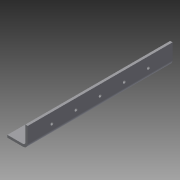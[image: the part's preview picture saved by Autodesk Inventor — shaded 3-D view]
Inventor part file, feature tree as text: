
AUTODESK INVENTOR PART (.ipt)
format: ipt  version: 2015 SP1 (Build 190203100, 203)  size: 133,632 bytes
history: native  units: in
note: dims shown in document units (in); Inventor stores cm internally (conversion verified against a paired STEP export)
features: sheet_metal_op x4, sketch x4, other x3, hole x2
ambient origin geometry x8: Origin, YZ Plane, XZ Plane, XY Plane, X Axis, Y Axis, Z Axis, Center Point
bodies: Solid1 (feature_tree)
feature tree (13):
  other  "<userpath>\Documents\2015 Offseason Chassis\West Coast Chassis Fall 2015\rivet(rv).xlsx"
  sheet_metal_op  "Face1"
  sheet_metal_op  "Flange1"
  hole  "Hole1"  [1 undecoded]
  hole  "Hole2"  [1 undecoded]
  sketch  "Sketch1"  dims[d0=1.0in d1=7.1in]
  other  "Plate1"
  sketch  "Sketch2"  dims[d2=0.12in d3=0.12in]
  other  "Plate2"
  sheet_metal_op  "Bend1"
  sheet_metal_op  "Corner1"
  sketch  "Sketch3"  dims[d4=0.06in]
  sketch  "Sketch4"  dims[d5=0.24in d6=0.12in d7=1.0in d8=90.0deg d9=0.12in d10=0.48in d11=0.12in d12=0.12in d13=0.5in d14=0.1406in d15=0.75in d16=0.375in d17=0.25in d18=0.5635in d19=0.12in d20=0.8108in d21=0.5in d22=0.1406in d23=0.75in d24=0.375in d25=0.25in d26=0.5635in d27=0.12in d28=0.8108in]
note: 2 required parameter values undecoded (feature->parameter linkage not recoverable at this tier; creation-order binding heuristic only, values carry confidence <= 0.55)
